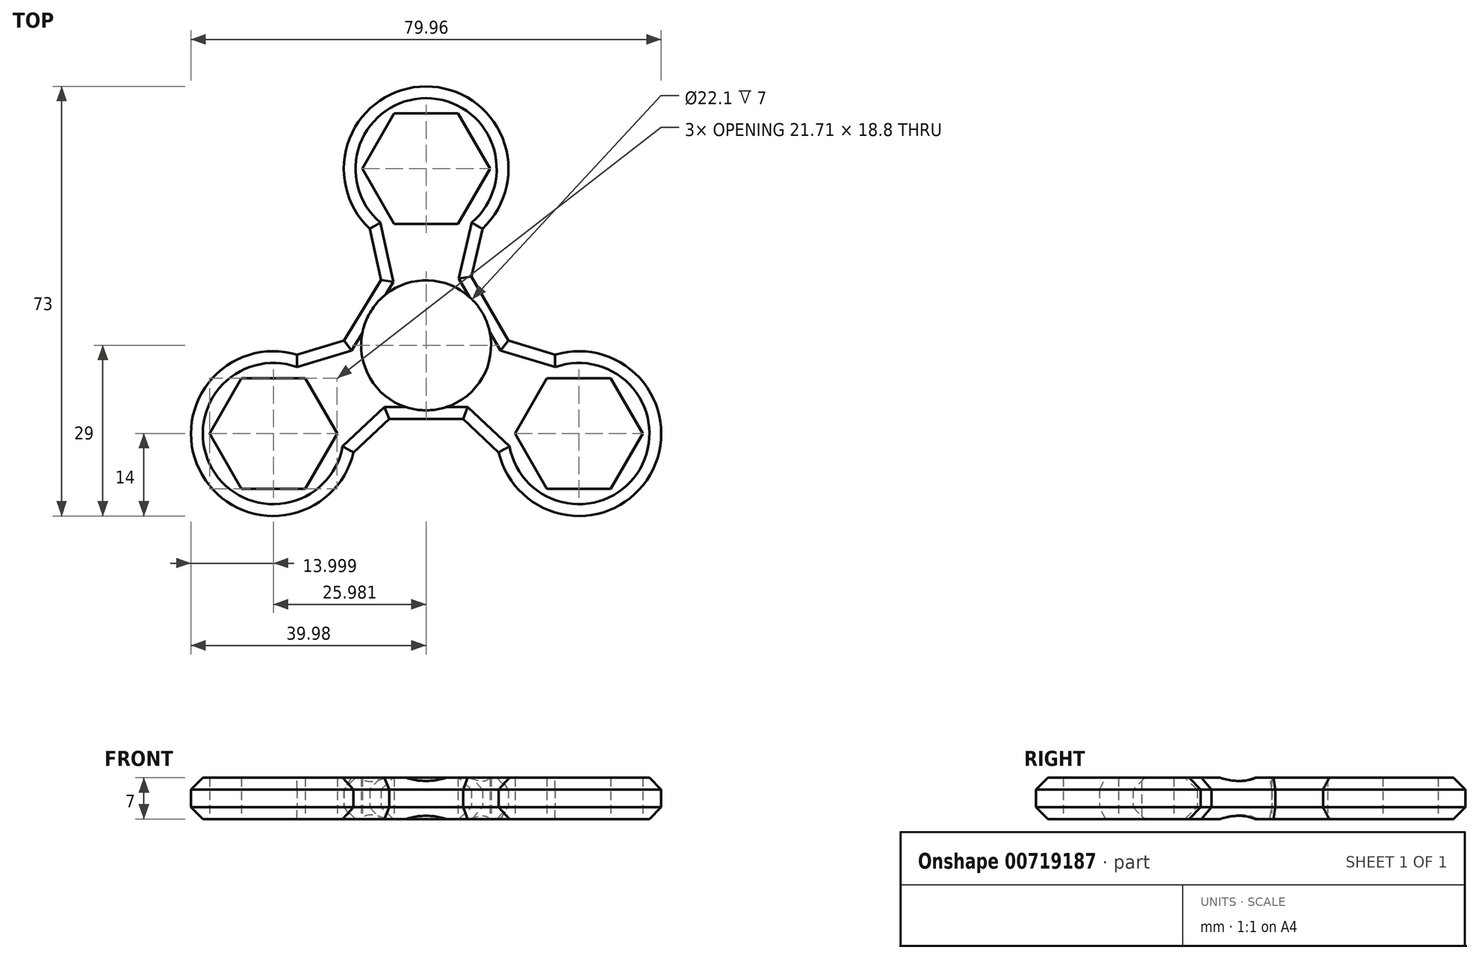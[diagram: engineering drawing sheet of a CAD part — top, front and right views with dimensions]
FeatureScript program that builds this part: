
annotation { "Feature Type Name" : "Feature", "Feature Type Description" : "" }
export const myFeature = defineFeature(function(context is Context, id is Id, definition is map)
    precondition{}
    {
        {
            var Q0;
            Q0=qCreatedBy(makeId("Top.planeOp"),FACE);
            var sketch = newSketch(context, id + "F0", { "sketchPlane" : qUnion([Q0])});
            skCircle(sketch, "E0", {"center": v(0, 0) * mm, "radius": 11.05 * mm});
            skArc(sketch, "E1", {"start": v(9.59, 19.8) * mm, "mid": v(0, 44) * mm, "end": v(-9.59, 19.8) * mm});
            skCircle(sketch, "E2.cCircle", {"center": v(0, 30) * mm, "radius": 9.4 * mm, "construction": true});
            skLineSegment(sketch, "E2.0", {"start": v(10.85, 30) * mm, "end": v(5.43, 20.6) * mm});
            skLineSegment(sketch, "E2.1", {"start": v(5.43, 20.6) * mm, "end": v(-5.43, 20.6) * mm});
            skLineSegment(sketch, "E2.2", {"start": v(-5.43, 20.6) * mm, "end": v(-10.85, 30) * mm});
            skLineSegment(sketch, "E2.3", {"start": v(-10.85, 30) * mm, "end": v(-5.43, 39.4) * mm});
            skLineSegment(sketch, "E2.4", {"start": v(-5.43, 39.4) * mm, "end": v(5.43, 39.4) * mm});
            skLineSegment(sketch, "E2.5", {"start": v(5.43, 39.4) * mm, "end": v(10.85, 30) * mm});
            skPoint(sketch, "E2.0.midPoint", {"position": v(8.14, 25.3) * mm});
            skLineSegment(sketch, "E3.1.0", {"start": v(-36.83, -15) * mm, "end": v(-31.4, -5.6) * mm});
            skLineSegment(sketch, "E3.1.1", {"start": v(-31.4, -24.4) * mm, "end": v(-36.83, -15) * mm});
            skLineSegment(sketch, "E3.1.2", {"start": v(-20.55, -24.4) * mm, "end": v(-31.4, -24.4) * mm});
            skLineSegment(sketch, "E3.1.3", {"start": v(-15.13, -15) * mm, "end": v(-20.55, -24.4) * mm});
            skPoint(sketch, "E3.1.4", {"position": v(-25.98, -5.6) * mm});
            skLineSegment(sketch, "E3.1.5", {"start": v(-20.55, -5.6) * mm, "end": v(-15.13, -15) * mm});
            skLineSegment(sketch, "E3.1.6", {"start": v(-31.4, -5.6) * mm, "end": v(-20.55, -5.6) * mm});
            skArc(sketch, "E3.1.7", {"start": v(-21.94, -1.6) * mm, "mid": v(-38.1, -22) * mm, "end": v(-12.35, -18.2) * mm});
            skCircle(sketch, "E3.1.8", {"center": v(-25.98, -15) * mm, "radius": 9.4 * mm, "construction": true});
            skLineSegment(sketch, "E3.2.0", {"start": v(31.4, -24.4) * mm, "end": v(20.55, -24.4) * mm});
            skLineSegment(sketch, "E3.2.1", {"start": v(36.83, -15) * mm, "end": v(31.4, -24.4) * mm});
            skLineSegment(sketch, "E3.2.2", {"start": v(31.4, -5.6) * mm, "end": v(36.83, -15) * mm});
            skLineSegment(sketch, "E3.2.3", {"start": v(20.55, -5.6) * mm, "end": v(31.4, -5.6) * mm});
            skPoint(sketch, "E3.2.4", {"position": v(17.84, -19.7) * mm});
            skLineSegment(sketch, "E3.2.5", {"start": v(15.13, -15) * mm, "end": v(20.55, -5.6) * mm});
            skLineSegment(sketch, "E3.2.6", {"start": v(20.55, -24.4) * mm, "end": v(15.13, -15) * mm});
            skArc(sketch, "E3.2.7", {"start": v(12.35, -18.2) * mm, "mid": v(38.1, -22) * mm, "end": v(21.94, -1.6) * mm});
            skCircle(sketch, "E3.2.8", {"center": v(25.98, -15) * mm, "radius": 9.4 * mm, "construction": true});
            skLineSegment(sketch, "E4", {"start": v(0, 30) * mm, "end": v(34.3, 10.2) * mm, "construction": true});
            skLineSegment(sketch, "E5", {"start": v(25.98, -15) * mm, "end": v(25.98, 19.7) * mm, "construction": true});
            skLineSegment(sketch, "E6", {"start": v(0, 0) * mm, "end": v(0, 0) * mm});
            skLineSegment(sketch, "E7", {"start": v(0, 0) * mm, "end": v(35.29, 20.37) * mm, "construction": true});
            skArc(sketch, "E8.trimOffspring", {"start": v(-7.7, 11.7) * mm, "mid": v(-7.75, 11.66) * mm, "end": v(-7.8, 11.62) * mm});
            skLineSegment(sketch, "E9", {"start": v(-6.28, -12.51) * mm, "end": v(-12.35, -18.2) * mm});
            skLineSegment(sketch, "E10", {"start": v(-6.28, -12.51) * mm, "end": v(6.28, -12.51) * mm});
            skLineSegment(sketch, "E11", {"start": v(12.35, -18.2) * mm, "end": v(6.28, -12.51) * mm});
            skLineSegment(sketch, "E12", {"start": v(9.59, 19.8) * mm, "end": v(7.7, 11.7) * mm});
            skLineSegment(sketch, "E13", {"start": v(7.7, 11.7) * mm, "end": v(13.98, 0.81) * mm});
            skLineSegment(sketch, "E14", {"start": v(13.98, 0.81) * mm, "end": v(21.94, -1.6) * mm});
            skLineSegment(sketch, "E15", {"start": v(-9.59, 19.8) * mm, "end": v(-7.7, 11.12) * mm});
            skLineSegment(sketch, "E16", {"start": v(-7.7, 11.12) * mm, "end": v(-13.98, 0.81) * mm});
            skLineSegment(sketch, "E17", {"start": v(-21.94, -1.6) * mm, "end": v(-13.98, 0.81) * mm});
            skPoint(sketch, "E18.orphan", {"position": v(12.12, 23) * mm});
            skSolve(sketch);
        }
        {
            var Q0;
            Q0=makeQuery(id+"F0.imprint","IMPRINT",FACE,{"disambiguationData":[TD([[makeQuery(id+"F0.imprint","IMPRINT",EDGE,{"derivedFrom":sQuery(id+"F0.wireOp",EDGE,"E0")}),-1.0]])]});
            extrude(context, id + "F1", {"entities" : qUnion([Q0]), "depth" : 7 * mm, "offsetDistance" : 25 * mm});
        }
        {
            var Q0;
            Q0=makeQuery(id+"F1.opExtrude","CAP_EDGE",EDGE,{"disambiguationData":[OSD([sQuery(id+"F0.wireOp",EDGE,"E3.1.7")])],"isStart":true});
            var Q1;
            Q1=makeQuery(id+"F1.opExtrude","CAP_EDGE",EDGE,{"disambiguationData":[OSD([sQuery(id+"F0.wireOp",EDGE,"E17")])],"isStart":true});
            var Q2;
            Q2=makeQuery(id+"F1.opExtrude","CAP_EDGE",EDGE,{"disambiguationData":[OSD([sQuery(id+"F0.wireOp",EDGE,"E16")])],"isStart":true});
            var Q3;
            Q3=makeQuery(id+"F1.opExtrude","CAP_EDGE",EDGE,{"disambiguationData":[OSD([sQuery(id+"F0.wireOp",EDGE,"E17")])],"isStart":false});
            var Q4;
            Q4=makeQuery(id+"F1.opExtrude","CAP_EDGE",EDGE,{"disambiguationData":[OSD([sQuery(id+"F0.wireOp",EDGE,"E16")])],"isStart":false});
            var Q5;
            Q5=makeQuery(id+"F1.opExtrude","CAP_EDGE",EDGE,{"disambiguationData":[OSD([sQuery(id+"F0.wireOp",EDGE,"E3.1.7")])],"isStart":false});
            var Q6;
            Q6=makeQuery(id+"F1.opExtrude","CAP_EDGE",EDGE,{"disambiguationData":[OSD([sQuery(id+"F0.wireOp",EDGE,"E15")])],"isStart":true});
            var Q7;
            Q7=makeQuery(id+"F1.opExtrude","CAP_EDGE",EDGE,{"disambiguationData":[OSD([sQuery(id+"F0.wireOp",EDGE,"E1")])],"isStart":true});
            var Q8;
            Q8=makeQuery(id+"F1.opExtrude","CAP_EDGE",EDGE,{"disambiguationData":[OSD([sQuery(id+"F0.wireOp",EDGE,"E12")])],"isStart":true});
            var Q9;
            Q9=makeQuery(id+"F1.opExtrude","CAP_EDGE",EDGE,{"disambiguationData":[OSD([sQuery(id+"F0.wireOp",EDGE,"E13")])],"isStart":true});
            var Q10;
            Q10=makeQuery(id+"F1.opExtrude","CAP_EDGE",EDGE,{"disambiguationData":[OSD([sQuery(id+"F0.wireOp",EDGE,"E14")])],"isStart":true});
            var Q11;
            Q11=makeQuery(id+"F1.opExtrude","CAP_EDGE",EDGE,{"disambiguationData":[OSD([sQuery(id+"F0.wireOp",EDGE,"E3.2.7")])],"isStart":true});
            var Q12;
            Q12=makeQuery(id+"F1.opExtrude","CAP_EDGE",EDGE,{"disambiguationData":[OSD([sQuery(id+"F0.wireOp",EDGE,"E3.2.7")])],"isStart":false});
            var Q13;
            Q13=makeQuery(id+"F1.opExtrude","CAP_EDGE",EDGE,{"disambiguationData":[OSD([sQuery(id+"F0.wireOp",EDGE,"E14")])],"isStart":false});
            var Q14;
            Q14=makeQuery(id+"F1.opExtrude","CAP_EDGE",EDGE,{"disambiguationData":[OSD([sQuery(id+"F0.wireOp",EDGE,"E13")])],"isStart":false});
            var Q15;
            Q15=makeQuery(id+"F1.opExtrude","CAP_EDGE",EDGE,{"disambiguationData":[OSD([sQuery(id+"F0.wireOp",EDGE,"E11")])],"isStart":true});
            var Q16;
            Q16=makeQuery(id+"F1.opExtrude","CAP_EDGE",EDGE,{"disambiguationData":[OSD([sQuery(id+"F0.wireOp",EDGE,"E10")])],"isStart":true});
            var Q17;
            Q17=makeQuery(id+"F1.opExtrude","CAP_EDGE",EDGE,{"disambiguationData":[OSD([sQuery(id+"F0.wireOp",EDGE,"E9")])],"isStart":true});
            var Q18;
            Q18=makeQuery(id+"F1.opExtrude","CAP_EDGE",EDGE,{"disambiguationData":[OSD([sQuery(id+"F0.wireOp",EDGE,"E1")])],"isStart":false});
            var Q19;
            Q19=makeQuery(id+"F1.opExtrude","CAP_EDGE",EDGE,{"disambiguationData":[OSD([sQuery(id+"F0.wireOp",EDGE,"E9")])],"isStart":false});
            var Q20;
            Q20=makeQuery(id+"F1.opExtrude","CAP_EDGE",EDGE,{"disambiguationData":[OSD([sQuery(id+"F0.wireOp",EDGE,"E10")])],"isStart":false});
            var Q21;
            Q21=makeQuery(id+"F1.opExtrude","CAP_EDGE",EDGE,{"disambiguationData":[OSD([sQuery(id+"F0.wireOp",EDGE,"E11")])],"isStart":false});
            var Q22;
            Q22=makeQuery(id+"F1.opExtrude","CAP_EDGE",EDGE,{"disambiguationData":[OSD([sQuery(id+"F0.wireOp",EDGE,"E12")])],"isStart":false});
            var Q23;
            Q23=makeQuery(id+"F1.opExtrude","CAP_EDGE",EDGE,{"disambiguationData":[OSD([sQuery(id+"F0.wireOp",EDGE,"E15")])],"isStart":false});
            chamfer(context, id + "F2", {"entities" : qUnion([Q0, Q1, Q2, Q3, Q4, Q5, Q6, Q7, Q8, Q9, Q10, Q11, Q12, Q13, Q14, Q15, Q16, Q17, Q18, Q19, Q20, Q21, Q22, Q23]), "width" : 2 * mm, "tangentPropagation" : true});
        }
    });
